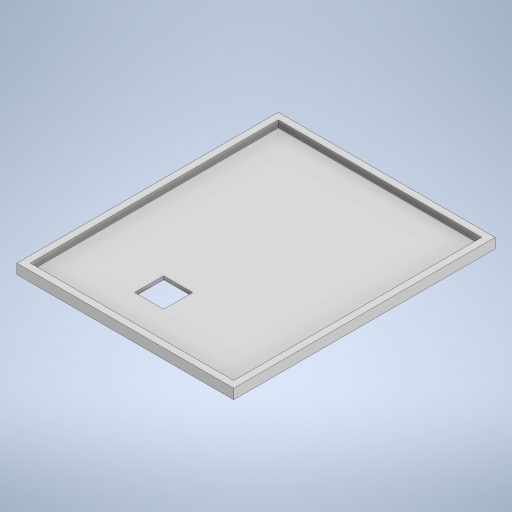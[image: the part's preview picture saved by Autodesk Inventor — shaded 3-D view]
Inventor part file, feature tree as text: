
AUTODESK INVENTOR PART (.ipt)
format: ipt  version: 2024 (Build 280153000, 153)  size: 579,584 bytes
history: native  units: mm
features: extrude x3, other x1
ambient origin geometry x8: Origin, YZ Plane, XZ Plane, XY Plane, X Axis, Y Axis, Z Axis, Center Point
bodies: Body1 (feature_tree)
feature tree (4):
  other  "Sólido1"
  extrude  "Extrusão1"  Depth=3.0mm
  extrude  "Extrusão2"  Depth=3.0mm
  extrude  "Extrusão3"  Depth=3.0mm
